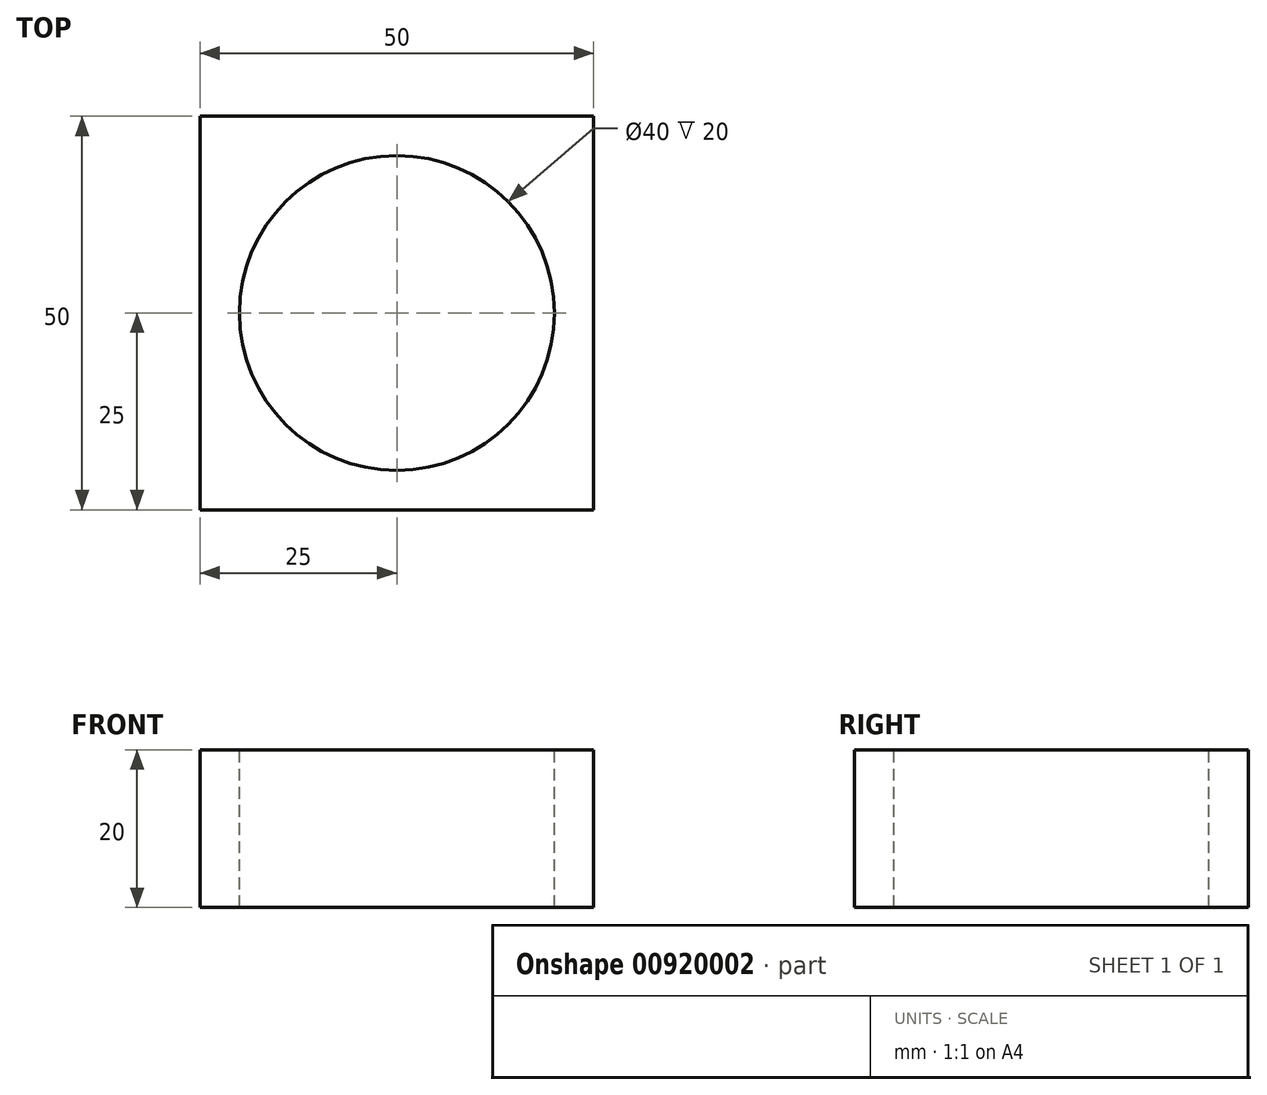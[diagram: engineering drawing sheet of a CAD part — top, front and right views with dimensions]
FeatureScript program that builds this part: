
annotation { "Feature Type Name" : "Feature", "Feature Type Description" : "" }
export const myFeature = defineFeature(function(context is Context, id is Id, definition is map)
    precondition{}
    {
        {
            var Q0;
            Q0=qCreatedBy(makeId("Top.planeOp"),FACE);
            var sketch = newSketch(context, id + "F0", { "sketchPlane" : qUnion([Q0])});
            skLineSegment(sketch, "E0.bottom", {"start": v(-50, 50) * mm, "end": v(50, 50) * mm});
            skLineSegment(sketch, "E0.top", {"start": v(-50, -50) * mm, "end": v(50, -50) * mm});
            skLineSegment(sketch, "E0.left", {"start": v(-50, 50) * mm, "end": v(-50, -50) * mm});
            skLineSegment(sketch, "E0.right", {"start": v(50, 50) * mm, "end": v(50, -50) * mm});
            skPoint(sketch, "E0.middle", {"position": v(0, 0) * mm});
            skLineSegment(sketch, "E1.bottom", {"start": v(-25, 25) * mm, "end": v(25, 25) * mm});
            skLineSegment(sketch, "E1.top", {"start": v(-25, -25) * mm, "end": v(25, -25) * mm});
            skLineSegment(sketch, "E1.left", {"start": v(-25, 25) * mm, "end": v(-25, -25) * mm});
            skLineSegment(sketch, "E1.right", {"start": v(25, 25) * mm, "end": v(25, -25) * mm});
            skSolve(sketch);
        }
        {
            var Q0;
            Q0=makeQuery(id+"F0.imprint","IMPRINT",FACE,{"disambiguationData":[TD([[makeQuery(id+"F0.imprint","IMPRINT",EDGE,{"derivedFrom":sQuery(id+"F0.wireOp",EDGE,"E1.bottom")}),-1.0]])]});
            extrude(context, id + "F1", {"entities" : qUnion([Q0]), "depth" : 20 * mm, "offsetDistance" : 25 * mm});
        }
        {
            var Q0;
            Q0=makeQuery(id+"F1.opExtrude","CAP_FACE",FACE,{"disambiguationData":[OSD([sQuery(id+"F0.wireOp",EDGE,"E1.bottom"),sQuery(id+"F0.wireOp",EDGE,"E1.top"),sQuery(id+"F0.wireOp",EDGE,"E1.left"),sQuery(id+"F0.wireOp",EDGE,"E1.right")])],"isStart":false});
            var sketch = newSketch(context, id + "F2", { "sketchPlane" : qUnion([Q0])});
            skPoint(sketch, "E2", {"position": v(0, 0) * mm});
            skSolve(sketch);
        }
        {
            var Q0;
            Q0=sQuery(id+"F2.wireOp",VERTEX,"E2");
            var Q1;
            Q1=makeQuery(id+"F1.opExtrude","SWEPT_BODY",BODY,{"disambiguationData":[OSD([sQuery(id+"F0.wireOp",EDGE,"E1.bottom"),sQuery(id+"F0.wireOp",EDGE,"E1.top"),sQuery(id+"F0.wireOp",EDGE,"E1.left"),sQuery(id+"F0.wireOp",EDGE,"E1.right")])]});
            hole(context, id + "F3", {"style" : HoleStyle.SIMPLE, "endStyle" : HoleEndStyle.THROUGH, "holeDiameter" : 40 * mm, "majorDiameter" : 5 * mm, "isTappedThrough" : true, "tappedDepth" : 12 * mm, "tapClearance" : 3, "startFromSketch" : true, "locations" : qUnion([Q0]), "scope" : qUnion([Q1])});
        }
    });
